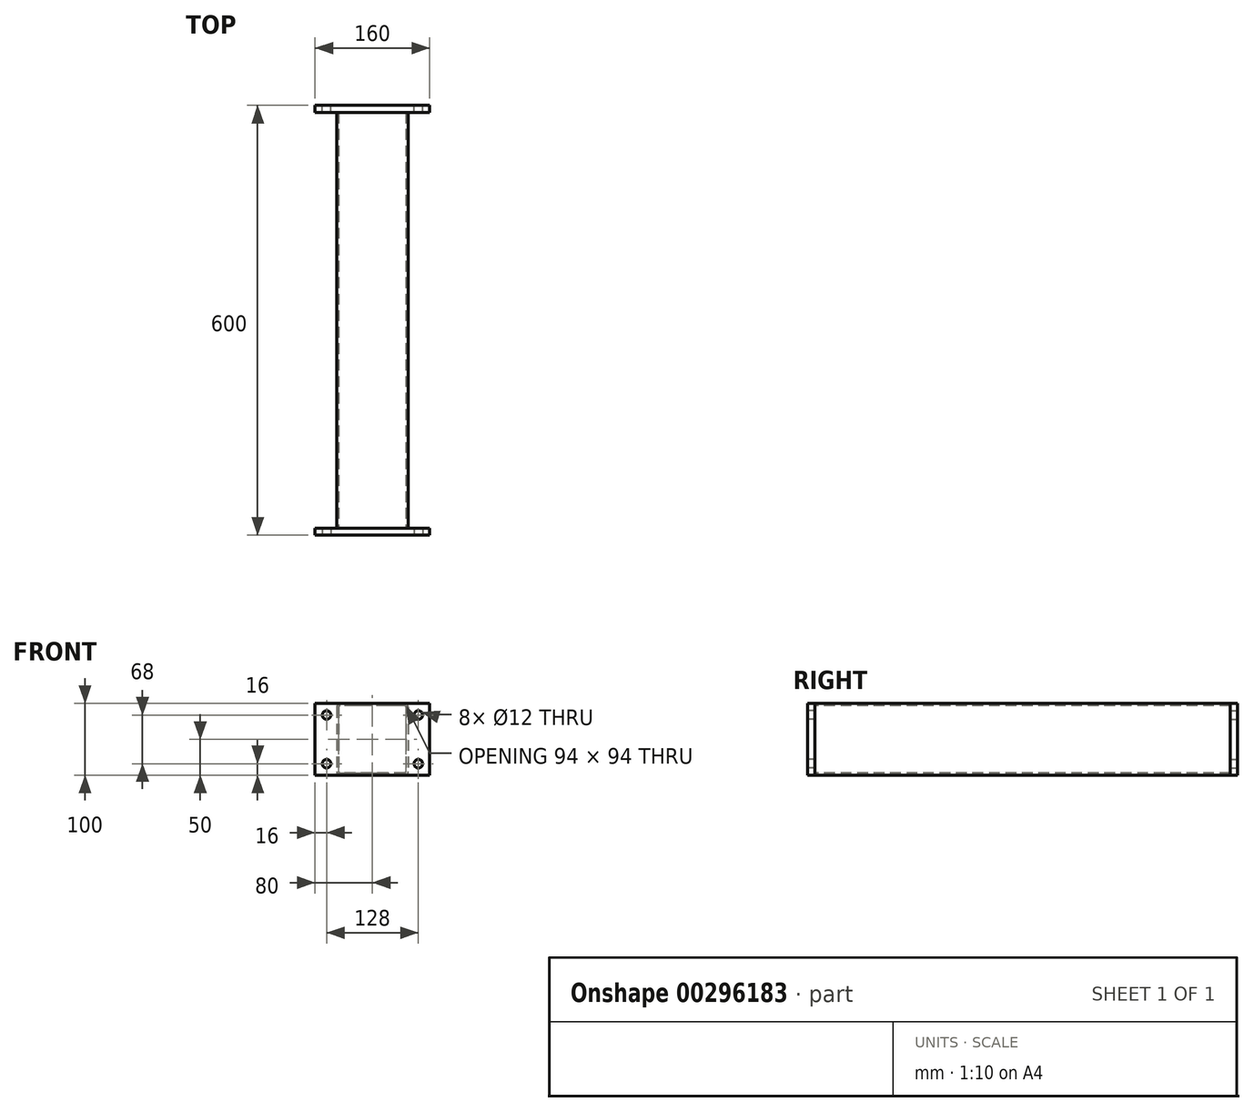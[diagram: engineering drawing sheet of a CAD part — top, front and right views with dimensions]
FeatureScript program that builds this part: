
annotation { "Feature Type Name" : "Feature", "Feature Type Description" : "" }
export const myFeature = defineFeature(function(context is Context, id is Id, definition is map)
    precondition{}
    {
        {
            var Q0;
            Q0=qCreatedBy(makeId("Front.planeOp"),FACE);
            var sketch = newSketch(context, id + "F0", { "sketchPlane" : qUnion([Q0])});
            skLineSegment(sketch, "E0.bottom", {"start": v(45, 50) * mm, "end": v(-45, 50) * mm});
            skLineSegment(sketch, "E0.top", {"start": v(45, -50) * mm, "end": v(-45, -50) * mm});
            skLineSegment(sketch, "E0.left", {"start": v(50, 45) * mm, "end": v(50, -45) * mm});
            skLineSegment(sketch, "E0.right", {"start": v(-50, 45) * mm, "end": v(-50, -45) * mm});
            skPoint(sketch, "E0.middle", {"position": v(0, 0) * mm});
            skPoint(sketch, "E1.visualSharp", {"position": v(-50, 50) * mm});
            skArc(sketch, "E1.filletArc", {"start": v(-45, 50) * mm, "mid": v(-48.54, 48.54) * mm, "end": v(-50, 45) * mm});
            skPoint(sketch, "E2.visualSharp", {"position": v(50, 50) * mm});
            skArc(sketch, "E2.filletArc", {"start": v(50, 45) * mm, "mid": v(48.54, 48.54) * mm, "end": v(45, 50) * mm});
            skPoint(sketch, "E3.visualSharp", {"position": v(50, -50) * mm});
            skArc(sketch, "E3.filletArc", {"start": v(45, -50) * mm, "mid": v(48.54, -48.54) * mm, "end": v(50, -45) * mm});
            skPoint(sketch, "E4.visualSharp", {"position": v(-50, -50) * mm});
            skArc(sketch, "E4.filletArc", {"start": v(-50, -45) * mm, "mid": v(-48.54, -48.54) * mm, "end": v(-45, -50) * mm});
            skArc(sketch, "E5.0", {"start": v(-45, 47) * mm, "mid": v(-46.41, 46.41) * mm, "end": v(-47, 45) * mm});
            skLineSegment(sketch, "E5.1", {"start": v(45, 47) * mm, "end": v(-45, 47) * mm});
            skLineSegment(sketch, "E5.2", {"start": v(-47, 45) * mm, "end": v(-47, -45) * mm});
            skArc(sketch, "E5.3", {"start": v(47, 45) * mm, "mid": v(46.41, 46.41) * mm, "end": v(45, 47) * mm});
            skArc(sketch, "E5.4", {"start": v(-47, -45) * mm, "mid": v(-46.41, -46.41) * mm, "end": v(-45, -47) * mm});
            skLineSegment(sketch, "E5.5", {"start": v(45, -47) * mm, "end": v(-45, -47) * mm});
            skArc(sketch, "E5.6", {"start": v(45, -47) * mm, "mid": v(46.41, -46.41) * mm, "end": v(47, -45) * mm});
            skLineSegment(sketch, "E5.7", {"start": v(47, 45) * mm, "end": v(47, -45) * mm});
            skSolve(sketch);
        }
        {
            var Q0;
            Q0=makeQuery(id+"F0.imprint","IMPRINT",FACE,{"disambiguationData":[TD([[makeQuery(id+"F0.imprint","IMPRINT",EDGE,{"derivedFrom":sQuery(id+"F0.wireOp",EDGE,"E0.bottom")}),1.0]])]});
            extrude(context, id + "F1", {"entities" : qUnion([Q0]), "oppositeDirection" : true, "depth" : (600 - 2 * 10) * mm});
        }
        {
            var Q0;
            Q0=qCreatedBy(makeId("Front.planeOp"),FACE);
            cPlane(context, id + "F2", {"entities" : qUnion([Q0]), "cplaneType" : CPlaneType.OFFSET, "offset" : 10 * mm, "width" : 150 * mm, "height" : 150 * mm});
        }
        {
            var Q0;
            Q0=qCreatedBy(id+"F2.planeOp",FACE);
            var sketch = newSketch(context, id + "F3", { "sketchPlane" : qUnion([Q0])});
            skLineSegment(sketch, "E6.bottom", {"start": v(-80, 50) * mm, "end": v(80, 50) * mm});
            skLineSegment(sketch, "E6.top", {"start": v(-80, -50) * mm, "end": v(80, -50) * mm});
            skLineSegment(sketch, "E6.left", {"start": v(-80, 50) * mm, "end": v(-80, -50) * mm});
            skLineSegment(sketch, "E6.right", {"start": v(80, 50) * mm, "end": v(80, -50) * mm});
            skPoint(sketch, "E6.middle", {"position": v(0, 0) * mm});
            skCircle(sketch, "E7", {"center": v(-64, 34) * mm, "radius": 6 * mm});
            skCircle(sketch, "E8", {"center": v(-64, -34) * mm, "radius": 6 * mm});
            skCircle(sketch, "E9", {"center": v(64, -34) * mm, "radius": 6 * mm});
            skCircle(sketch, "E10", {"center": v(64, 34) * mm, "radius": 6 * mm});
            skSolve(sketch);
        }
        {
            var Q0;
            Q0=makeQuery(id+"F3.imprint","IMPRINT",FACE,{"disambiguationData":[TD([[makeQuery(id+"F3.imprint","IMPRINT",EDGE,{"derivedFrom":sQuery(id+"F3.wireOp",EDGE,"E6.bottom")}),-1.0]])]});
            extrude(context, id + "F4", {"entities" : qUnion([Q0]), "oppositeDirection" : true, "depth" : 10 * mm});
        }
        {
            var Q0;
            Q0=makeQuery(id+"F1.opExtrude","CAP_FACE",FACE,{"disambiguationData":[OSD([sQuery(id+"F0.wireOp",EDGE,"E0.bottom"),sQuery(id+"F0.wireOp",EDGE,"E0.top"),sQuery(id+"F0.wireOp",EDGE,"E0.left"),sQuery(id+"F0.wireOp",EDGE,"E0.right"),sQuery(id+"F0.wireOp",EDGE,"E1.filletArc"),sQuery(id+"F0.wireOp",EDGE,"E2.filletArc"),sQuery(id+"F0.wireOp",EDGE,"E3.filletArc"),sQuery(id+"F0.wireOp",EDGE,"E4.filletArc"),sQuery(id+"F0.wireOp",EDGE,"E5.0"),sQuery(id+"F0.wireOp",EDGE,"E5.1"),sQuery(id+"F0.wireOp",EDGE,"E5.2"),sQuery(id+"F0.wireOp",EDGE,"E5.3"),sQuery(id+"F0.wireOp",EDGE,"E5.4"),sQuery(id+"F0.wireOp",EDGE,"E5.5"),sQuery(id+"F0.wireOp",EDGE,"E5.6"),sQuery(id+"F0.wireOp",EDGE,"E5.7")])],"isStart":false});
            cPlane(context, id + "F5", {"entities" : qUnion([Q0]), "cplaneType" : CPlaneType.OFFSET, "offset" : 10 * mm, "width" : 150 * mm, "height" : 150 * mm});
        }
        {
            var Q0;
            Q0=qCreatedBy(id+"F5.planeOp",FACE);
            var sketch = newSketch(context, id + "F6", { "sketchPlane" : qUnion([Q0])});
            skLineSegment(sketch, "E11.bottom", {"start": v(-80, 50) * mm, "end": v(80, 50) * mm});
            skLineSegment(sketch, "E11.top", {"start": v(-80, -50) * mm, "end": v(80, -50) * mm});
            skLineSegment(sketch, "E11.left", {"start": v(-80, 50) * mm, "end": v(-80, -50) * mm});
            skLineSegment(sketch, "E11.right", {"start": v(80, 50) * mm, "end": v(80, -50) * mm});
            skPoint(sketch, "E11.middle", {"position": v(0, 0) * mm});
            skCircle(sketch, "E12", {"center": v(-64, 34) * mm, "radius": 6 * mm});
            skCircle(sketch, "E13", {"center": v(-64, -34) * mm, "radius": 6 * mm});
            skCircle(sketch, "E14", {"center": v(64, -34) * mm, "radius": 6 * mm});
            skCircle(sketch, "E15", {"center": v(64, 34) * mm, "radius": 6 * mm});
            skSolve(sketch);
        }
        {
            var Q0;
            Q0=makeQuery(id+"F6.imprint","IMPRINT",FACE,{"disambiguationData":[TD([[makeQuery(id+"F6.imprint","IMPRINT",EDGE,{"derivedFrom":sQuery(id+"F6.wireOp",EDGE,"E11.bottom")}),-1.0]])]});
            extrude(context, id + "F7", {"entities" : qUnion([Q0]), "oppositeDirection" : true, "depth" : 10 * mm});
        }
    });
